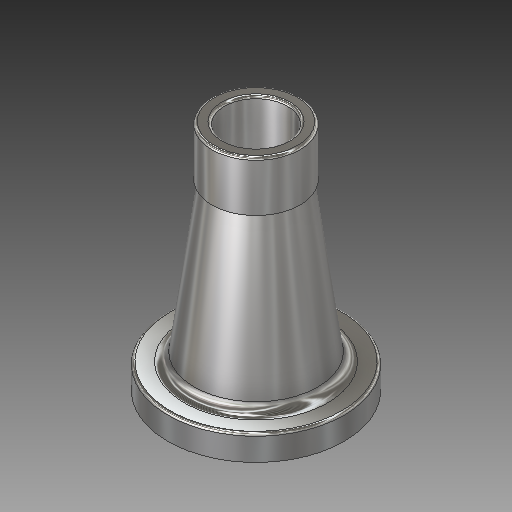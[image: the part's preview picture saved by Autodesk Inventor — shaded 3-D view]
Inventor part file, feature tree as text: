
AUTODESK INVENTOR PART (.ipt)
format: ipt  version: 2018 (Build 220112000, 112)  size: 223,744 bytes
history: native  units: in
note: dims shown in document units (in); Inventor stores cm internally (conversion verified against a paired STEP export)
features: fillet x4, revolve x1, sketch x1
ambient origin geometry x8: Origin, YZ Plane, XZ Plane, XY Plane, X Axis, Y Axis, Z Axis, Center Point
bodies: Solid1 (feature_tree)
feature tree (6):
  revolve  "Revolution1"  [1 undecoded]
  fillet  "Fillet1"  Radius=0.7874in
  fillet  "Fillet2"  Radius=0.7874in
  fillet  "Fillet3"  Radius=0.3937in
  fillet  "Fillet4"  Radius=1.5748in
  sketch  "Sketch1"  dims[d0=0.7874in d1=0.1181in d2=0.7874in d3=0.7874in d4=0.3937in d5=1.5748in d6=0.0787in d7=90.0deg d8=0.0787in d9=0.0787in d10=0.0787in d15=0.315in]
note: 1 required parameter value undecoded (feature->parameter linkage not recoverable at this tier; creation-order binding heuristic only, values carry confidence <= 0.55)
